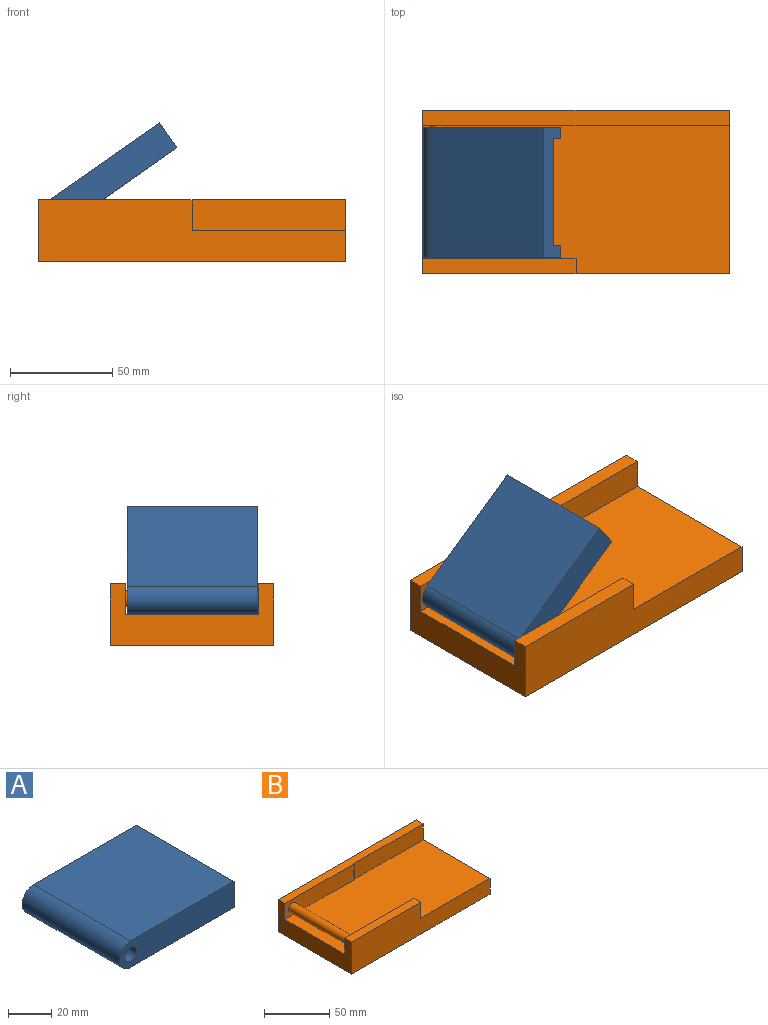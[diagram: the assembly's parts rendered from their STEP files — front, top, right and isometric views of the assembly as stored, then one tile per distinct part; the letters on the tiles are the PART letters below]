
ASSEMBLY  parts=2 mates=1
PART A: 11 faces, bbox 75.2x64x15 mm
  f0: plane 67.7x64mm, normal (0,0,-1), area 949.9mm2, adj f2,f3,f4,f5,f7,f9,f10
  f1: plane 67.7x64mm, normal (0,0,1), area 4333.1mm2, adj f2,f3,f7,f10
  f2: plane 75.2x15mm, normal (0,-1,0), area 1053.7mm2, adj f0,f1,f7,f8,f10
  f3: plane 75.2x15mm, normal (0,1,0), area 1053.7mm2, adj f0,f1,f7,f8,f10
  f4: plane 64.52x6.3mm, normal (0,-1,0), area 406mm2, adj f0,f6,f8,f9,f10
  f5: plane 64.52x6.3mm, normal (0,1,0), area 406mm2, adj f0,f6,f8,f9,f10
  f6: plane 63.89x52.44mm, normal (0,0,-1), area 3350.4mm2, adj f4,f5,f8,f10
  f7: cylinder r=7.5mm len=64mm, axis (0,1,0), area 1508mm2, adj f0,f1,f2,f3
  f8: cylinder r=4mm len=64mm, axis (0,1,0), area 1536.5mm2, adj f2,f3,f4,f5,f6,f9
  f9: plane 52.44x5.09mm, normal (1,0,0), area 266.7mm2, adj f0,f4,f5,f8
  f10: plane 64x15mm, normal (1,0,0), area 629.6mm2, adj f0,f1,f2,f3,f4,f5,f6
PART B: 14 faces, bbox 150x80x30 mm
  f0: plane 150x30mm, normal (0,-1,0), area 3375mm2, adj f1,f4,f6,f8,f9,f13
  f1: plane 75x7.5mm, normal (0,0,1), area 562.5mm2, adj f0,f3,f6,f13
  f2: plane 75x15mm, normal (0,-1,0), area 1074.7mm2, adj f6,f7,f9,f10,f11
  f3: plane 75x15mm, normal (0,1,0), area 1074.7mm2, adj f1,f6,f9,f10,f13
  f4: plane 80x30mm, normal (1,0,0), area 1310.7mm2, adj f0,f5,f7,f8,f9,f12
  f5: plane 150x30mm, normal (0,1,0), area 4500mm2, adj f4,f6,f7,f8
  f6: plane 80x30mm, normal (-1,0,0), area 1425mm2, adj f0,f1,f2,f3,f5,f7,f8,f9
  f7: plane 150x7.5mm, normal (0,0,1), area 1116mm2, adj f2,f4,f5,f6,f11,f12
  f8: plane 150x80mm, normal (0,0,-1), area 12000mm2, adj f0,f4,f5,f6
  f9: plane 150x72.62mm, normal (0,0,1), area 10321.5mm2, adj f0,f2,f3,f4,f6,f11,f12,f13
  f10: cylinder r=4mm len=65mm, axis (0,1,0), area 1633.6mm2, adj f2,f3
  f11: plane 15x0.12mm, normal (1,0,0), area 1.8mm2, adj f2,f7,f9,f12
  f12: plane 75x15mm, normal (0,-1,0), area 1125mm2, adj f4,f7,f9,f11
  f13: plane 15x7.5mm, normal (1,0,0), area 112.5mm2, adj f0,f1,f3,f9
PLACE A rot(axis=(0,-1,0),35deg) t=(4.79,-30.3,58.94)mm
PLACE B t=(3.51,-30,30.9)mm fixed
MATE cylindrical B.f10 <-> A.f7  axis (0,1,0) through (-63.69,-30,38.7)mm
